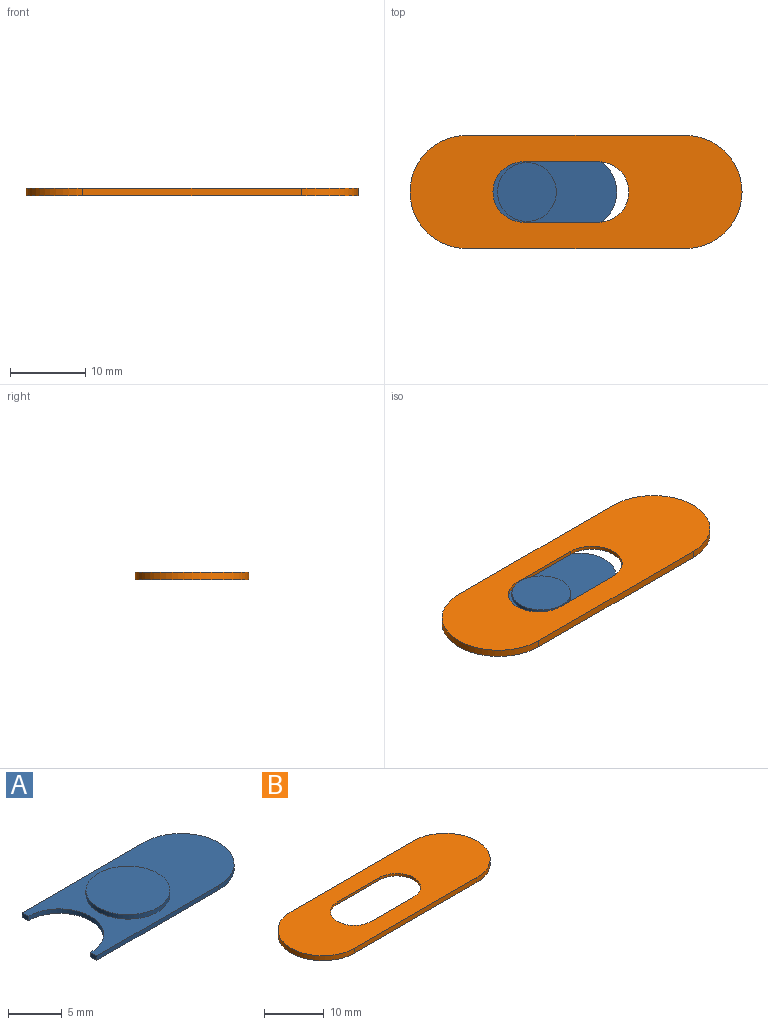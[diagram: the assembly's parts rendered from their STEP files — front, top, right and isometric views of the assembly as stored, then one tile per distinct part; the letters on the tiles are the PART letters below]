
ASSEMBLY  parts=2 mates=1
PART A: 10 faces, bbox 20.9x9.8x1 mm
  f0: plane 0.8x0.5mm, normal (-1,0,0), area 0.4mm2, adj f1,f5,f6,f7
  f1: plane 16x0.5mm, normal (0,-1,0), area 8mm2, adj f0,f2,f6,f7
  f2: cylinder r=4.9mm len=9.8mm, axis (0,0,-1), area 7.7mm2, adj f1,f3,f6,f7
  f3: plane 16x0.5mm, normal (0,1,0), area 8mm2, adj f2,f4,f6,f7
  f4: plane 0.8x0.5mm, normal (-1,0,0), area 0.4mm2, adj f3,f5,f6,f7
  f5: cylinder r=4.1mm len=8.2mm, axis (0,0,-1), area 6.4mm2, adj f0,f4,f6,f7
  f6: plane 20.9x9.8mm, normal (0,0,1), area 120.3mm2, adj f0,f1,f2,f3,f4,f5,f8
  f7: plane 20.9x9.8mm, normal (0,0,-1), area 168.1mm2, adj f0,f1,f2,f3,f4,f5
  f8: cylinder r=3.9mm len=7.8mm, axis (0,0,-1), area 12.3mm2, adj f6,f9
  f9: plane 7.8x7.8mm, normal (0,0,1), area 47.8mm2, adj f8
PART B: 17 faces, bbox 44x15x1 mm
  f0: cylinder r=4mm len=8mm, axis (0,0,-1), area 6.3mm2, adj f1,f3,f9,f16
  f1: plane 10x0.5mm, normal (0,-1,0), area 5mm2, adj f0,f2,f9,f16
  f2: cylinder r=4mm len=8mm, axis (0,0,-1), area 6.3mm2, adj f1,f3,f9,f16
  f3: plane 10x0.5mm, normal (0,1,0), area 5mm2, adj f0,f2,f9,f16
  f4: plane 44x15mm, normal (0,0,-1), area 347.6mm2, adj f5,f6,f7,f8,f10,f11,f12,f13
  f5: cylinder r=7.5mm len=15mm, axis (0,0,-1), area 23.6mm2, adj f4,f6,f8,f9
  f6: plane 29x1mm, normal (0,-1,0), area 29mm2, adj f4,f5,f7,f9
  f7: cylinder r=7.5mm len=15mm, axis (0,0,-1), area 23.6mm2, adj f4,f6,f8,f9
  f8: plane 29x1mm, normal (0,1,0), area 29mm2, adj f4,f5,f7,f9
  f9: plane 44x15mm, normal (0,0,1), area 481.4mm2, adj f0,f1,f2,f3,f5,f6,f7,f8
  f10: plane 25x0.5mm, normal (0,1,0), area 12.5mm2, adj f4,f11,f15,f16
  f11: plane 1x0.5mm, normal (1,0,0), area 0.5mm2, adj f4,f10,f12,f16
  f12: cylinder r=4mm len=8mm, axis (0,0,-1), area 6.3mm2, adj f4,f11,f13,f16
  f13: plane 1x0.5mm, normal (1,0,0), area 0.5mm2, adj f4,f12,f14,f16
  f14: plane 25x0.5mm, normal (0,-1,0), area 12.5mm2, adj f4,f13,f15,f16
  f15: cylinder r=5mm len=10mm, axis (0,0,-1), area 7.9mm2, adj f4,f10,f14,f16
  f16: plane 30x10mm, normal (0,0,-1), area 133.9mm2, adj f0,f1,f2,f3,f10,f11,f12,f13
PLACE A t=(-12.4,0,0)mm
PLACE B t=(-6.9,0,0)mm
MATE planar B.f11 <-> A.f0  axis (1,0,0) through (-20.4,-4.5,0.25)mm
